# Revit family: Legrand XL³ 125 cabinet door
name_source: partatom
category: Equipement électrique
revit_build: Autodesk Revit 2018 (Build: 20170223_1515(x64)
units: mm (PartAtom-declared; Revit-internal decimal feet)

## family parameters
Basée sur le plan de construction = Oui
Configuration du panneau = Deux colonnes, circuits au sein
Cote de connecteur circulaire = Utiliser le diamètre
Couper avec des vides une fois chargée = Non
Numéro OmniClass = 23.80.30.11.17
Partagée = Non
Point de calcul de pièce = Non
Titre OmniClass = Distribution Boards and Control Panels
Toujours verticalement = Non
Type d'élément = Tableau de raccordement

## types (8) — shared parameters
Color = RAL 9003
Elévation par défaut = 1219 mm
Fabricant = legrand
General Conditions of Use = https://export.legrand.com
IK = 09
IP = 40
Material = Polystyrene
Modèle = XL³ 125
depth = 27 mm  [stored 0.0885827 ft]
transparent door 401872 = Non
width = 450 mm  [stored 1.47638 ft]

## per-type parameters (varying)
| type | URL | height | transparent door 401871 | transparent door 401873 | transparent door 401874 | white door 401861 | white door 401862 | white door 401863 | white door 401864 |
| white door 401861 | www.bticino.com | 300 mm | Non | Non | Non | Oui | Non | Non | Non |
| white door 401862 | www.bticino.com | 450 mm  [stored 1.47638 ft] | Non | Non | Non | Non | Oui | Non | Non |
| white door 401863 | www.bticino.com | 600 mm | Non | Non | Non | Non | Non | Oui | Non |
| white door 401864 | www.legrand.com | 750 mm  [stored 2.46063 ft] | Non | Non | Non | Non | Non | Non | Oui |
| transparent door 401871 | www.bticino.com | 300 mm | Oui | Non | Non | Non | Non | Non | Non |
| transparent door 401872 | www.bticino.com | 300 mm | Non | Non | Non | Non | Non | Non | Non |
| transparent door 401873 | www.bticino.com | 300 mm | Non | Oui | Non | Non | Non | Non | Non |
| transparent door 401874 | www.bticino.com | 300 mm | Non | Non | Oui | Non | Non | Non | Non |

note: [stored X ft] marks values corroborated as IEEE doubles in the binary element streams (Revit-internal decimal feet)
